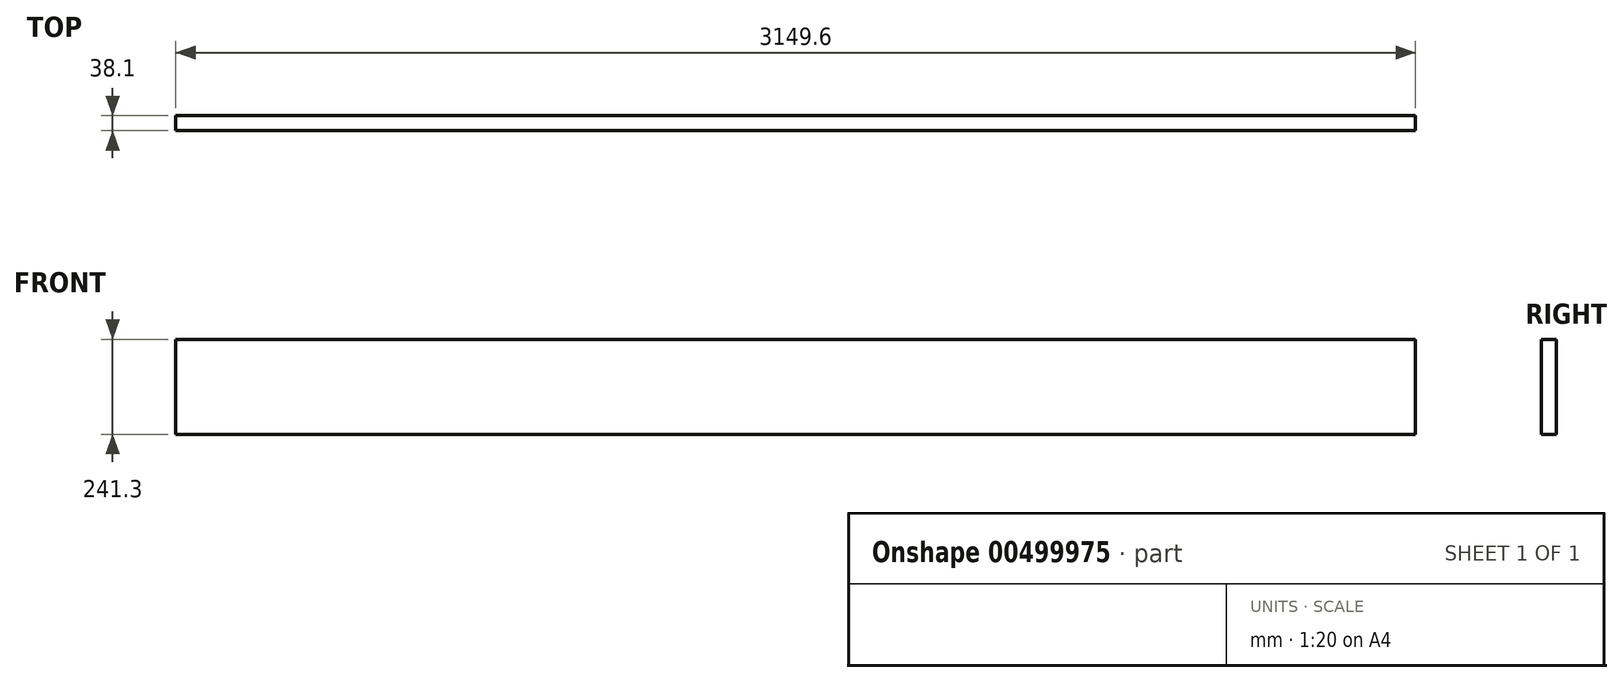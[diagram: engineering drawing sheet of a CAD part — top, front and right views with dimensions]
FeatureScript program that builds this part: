
annotation { "Feature Type Name" : "Feature", "Feature Type Description" : "" }
export const myFeature = defineFeature(function(context is Context, id is Id, definition is map)
    precondition{}
    {
        {
            var Q0;
            Q0=qCreatedBy(makeId("Front.planeOp"),FACE);
            var sketch = newSketch(context, id + "F0", { "sketchPlane" : qUnion([Q0])});
            skLineSegment(sketch, "E0.bottom", {"start": v(-1574.8, 120.65) * mm, "end": v(1574.8, 120.65) * mm});
            skLineSegment(sketch, "E0.top", {"start": v(-1574.8, -120.65) * mm, "end": v(1574.8, -120.65) * mm});
            skLineSegment(sketch, "E0.left", {"start": v(-1574.8, 120.65) * mm, "end": v(-1574.8, -120.65) * mm});
            skLineSegment(sketch, "E0.right", {"start": v(1574.8, 120.65) * mm, "end": v(1574.8, -120.65) * mm});
            skPoint(sketch, "E0.middle", {"position": v(0, 0) * mm});
            skSolve(sketch);
        }
        {
            var Q0;
            Q0=qSketchRegion(id+"F0",true);
            extrude(context, id + "F1", {"entities" : qUnion([Q0]), "depth" : 38.1 * mm, "offsetDistance" : 25.4 * mm});
        }
    });
